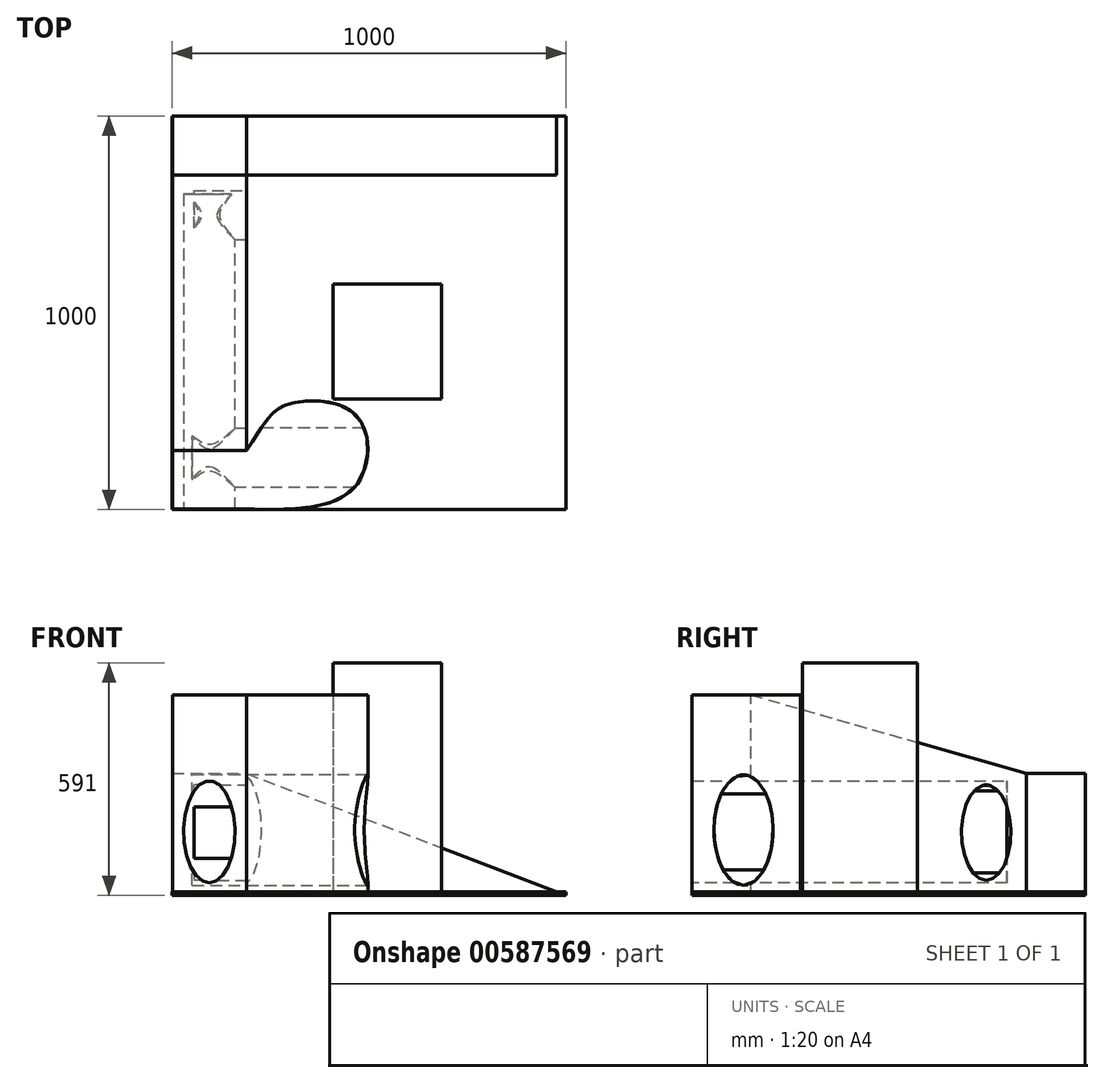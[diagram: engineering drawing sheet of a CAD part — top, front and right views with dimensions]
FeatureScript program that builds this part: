
annotation { "Feature Type Name" : "Feature", "Feature Type Description" : "" }
export const myFeature = defineFeature(function(context is Context, id is Id, definition is map)
    precondition{}
    {
        {
            var Q0;
            Q0=qCreatedBy(makeId("Top.planeOp"),FACE);
            var sketch = newSketch(context, id + "F0", { "sketchPlane" : qUnion([Q0])});
            skLineSegment(sketch, "E0.bottom", {"start": v(500, -500) * mm, "end": v(-500, -500) * mm});
            skLineSegment(sketch, "E0.top", {"start": v(500, 500) * mm, "end": v(-500, 500) * mm});
            skLineSegment(sketch, "E0.left", {"start": v(500, -500) * mm, "end": v(500, 500) * mm});
            skLineSegment(sketch, "E0.right", {"start": v(-500, -500) * mm, "end": v(-500, 500) * mm});
            skPoint(sketch, "E0.middle", {"position": v(0, 0) * mm});
            skSolve(sketch);
        }
        {
            var Q0;
            Q0=makeQuery(id+"F0.imprint","IMPRINT",FACE,{"disambiguationData":[TD([[makeQuery(id+"F0.imprint","IMPRINT",EDGE,{"derivedFrom":sQuery(id+"F0.wireOp",EDGE,"E0.bottom")}),-1.0]])]});
            extrude(context, id + "F1", {"entities" : qUnion([Q0]), "oppositeDirection" : true, "depth" : 10 * mm, "offsetDistance" : 25 * mm});
        }
        {
            var Q0;
            Q0=qCreatedBy(makeId("Front.planeOp"),FACE);
            cPlane(context, id + "F2", {"entities" : qUnion([Q0]), "cplaneType" : CPlaneType.OFFSET, "offset" : 500 * mm, "oppositeDirection" : true, "width" : 150 * mm, "height" : 150 * mm});
        }
        {
            var Q0;
            Q0=qCreatedBy(id+"F2.planeOp",FACE);
            var sketch = newSketch(context, id + "F3", { "sketchPlane" : qUnion([Q0])});
            skLineSegment(sketch, "E1", {"start": v(476.55, 0) * mm, "end": v(-310.9, 0) * mm});
            skLineSegment(sketch, "E2", {"start": v(-310.9, 0) * mm, "end": v(-310.9, 300) * mm});
            skLineSegment(sketch, "E3", {"start": v(-310.9, 300) * mm, "end": v(476.55, 0) * mm});
            skLineSegment(sketch, "E4", {"start": v(-310.9, 0) * mm, "end": v(-499.17, 0) * mm});
            skLineSegment(sketch, "E5", {"start": v(-499.17, 0) * mm, "end": v(-499.17, 300) * mm});
            skLineSegment(sketch, "E6", {"start": v(-499.17, 300) * mm, "end": v(-310.9, 300) * mm});
            skSolve(sketch);
        }
        {
            var Q0;
            Q0=makeQuery(id+"F3.imprint","IMPRINT",FACE,{"disambiguationData":[TD([[makeQuery(id+"F3.imprint","IMPRINT",EDGE,{"derivedFrom":sQuery(id+"F3.wireOp",EDGE,"E1")}),-1.0]])]});
            var Q1;
            Q1=makeQuery(id+"F3.imprint","IMPRINT",FACE,{"disambiguationData":[TD([[makeQuery(id+"F3.imprint","IMPRINT",EDGE,{"derivedFrom":sQuery(id+"F3.wireOp",EDGE,"E2")}),1.0]])]});
            extrude(context, id + "F4", {"entities" : qUnion([Q0, Q1]), "operationType" : NewBodyOperationType.ADD, "depth" : 150 * mm, "offsetDistance" : 25 * mm});
        }
        {
            var Q0;
            Q0=makeQuery(id+"F4.opExtrude","SWEPT_FACE",FACE,{"disambiguationData":[OSD([sQuery(id+"F3.wireOp",EDGE,"E5")])]});
            var sketch = newSketch(context, id + "F5", { "sketchPlane" : qUnion([Q0])});
            skLineSegment(sketch, "E7", {"start": v(-350, 300) * mm, "end": v(-350, 0) * mm});
            skLineSegment(sketch, "E8", {"start": v(-350, 0) * mm, "end": v(350, 0) * mm});
            skLineSegment(sketch, "E9", {"start": v(350, 0) * mm, "end": v(350, 500) * mm});
            skLineSegment(sketch, "E10", {"start": v(350, 500) * mm, "end": v(-350, 300) * mm});
            skLineSegment(sketch, "E11", {"start": v(350, 0) * mm, "end": v(499.02, 0) * mm});
            skLineSegment(sketch, "E12", {"start": v(499.02, 0) * mm, "end": v(499.02, 500) * mm});
            skLineSegment(sketch, "E13", {"start": v(499.02, 500) * mm, "end": v(350, 500) * mm});
            skSolve(sketch);
        }
        {
            var Q0;
            Q0=makeQuery(id+"F5.imprint","IMPRINT",FACE,{"disambiguationData":[TD([[makeQuery(id+"F5.imprint","IMPRINT",EDGE,{"derivedFrom":sQuery(id+"F5.wireOp",EDGE,"E7")}),-1.0]])]});
            var Q1;
            Q1=makeQuery(id+"F5.imprint","IMPRINT",FACE,{"disambiguationData":[TD([[makeQuery(id+"F5.imprint","IMPRINT",EDGE,{"derivedFrom":sQuery(id+"F5.wireOp",EDGE,"E9")}),-1.0]])]});
            extrude(context, id + "F6", {"entities" : qUnion([Q0, Q1]), "operationType" : NewBodyOperationType.ADD, "oppositeDirection" : true, "depth" : 188 * mm, "offsetDistance" : 25 * mm});
        }
        {
            var Q0;
            Q0=makeQuery(id+"F6.opExtrude","SWEPT_FACE",FACE,{"disambiguationData":[OSD([sQuery(id+"F5.wireOp",EDGE,"E13")])]});
            var sketch = newSketch(context, id + "F7", { "sketchPlane" : qUnion([Q0])});
            skFitSpline(sketch, "E14", {"points": [v(-311.17, -499.02) * mm, v(-35.43, -442.33) * mm, v(-31.14, -261.96) * mm, v(-185.74, -227.6) * mm, v(-239.42, -251.23) * mm, v(-267.33, -283.44) * mm, v(-311.17, -350) * mm], "startDerivative": vector(1320.7, -22.27) * mm, "endDerivative": vector(-342.1, -535.5) * mm});
            skSolve(sketch);
        }
        {
            var Q0;
            Q0=makeQuery(id+"F7.imprint","IMPRINT",FACE,{"disambiguationData":[TD([[makeQuery(id+"F7.imprint","IMPRINT",EDGE,{"derivedFrom":sQuery(id+"F7.wireOp",EDGE,"E14")}),1.0]])]});
            extrude(context, id + "F8", {"entities" : qUnion([Q0]), "operationType" : NewBodyOperationType.ADD, "oppositeDirection" : true, "depth" : 500 * mm, "offsetDistance" : 25 * mm});
        }
        {
            var Q0;
            Q0=makeQuery(id+"F6.opExtrude","CAP_FACE",FACE,{"disambiguationData":[OSD([sQuery(id+"F5.wireOp",EDGE,"E7"),sQuery(id+"F5.wireOp",EDGE,"E8"),sQuery(id+"F5.wireOp",EDGE,"E10"),sQuery(id+"F5.wireOp",EDGE,"E11"),sQuery(id+"F5.wireOp",EDGE,"E12"),sQuery(id+"F5.wireOp",EDGE,"E13")])],"isStart":false});
            cPlane(context, id + "F9", {"entities" : qUnion([Q0]), "cplaneType" : CPlaneType.OFFSET, "offset" : 315 * mm, "width" : 150 * mm, "height" : 150 * mm});
        }
        {
            var Q0;
            Q0=qCreatedBy(id+"F9.planeOp",FACE);
            var sketch = newSketch(context, id + "F10", { "sketchPlane" : qUnion([Q0])});
            skEllipse(sketch, "E15", {"center": v(-368.56, 156.63) * mm, "majorRadius": 140.2 * mm, "minorRadius": 75 * mm, "majorAxis": v(0, -1)});
            skSolve(sketch);
        }
        {
            var Q0;
            Q0=makeQuery(id+"F1.opExtrude","CAP_FACE",FACE,{"disambiguationData":[OSD([sQuery(id+"F0.wireOp",EDGE,"E0.bottom"),sQuery(id+"F0.wireOp",EDGE,"E0.top"),sQuery(id+"F0.wireOp",EDGE,"E0.left"),sQuery(id+"F0.wireOp",EDGE,"E0.right")])],"isStart":true});
            cPlane(context, id + "F11", {"entities" : qUnion([Q0]), "cplaneType" : CPlaneType.OFFSET, "offset" : 150 * mm, "width" : 150 * mm, "height" : 150 * mm});
        }
        {
            var Q0;
            Q0=makeQuery(id+"F10.imprint","IMPRINT",FACE,{"disambiguationData":[TD([[makeQuery(id+"F10.imprint","IMPRINT",EDGE,{"derivedFrom":sQuery(id+"F10.wireOp",EDGE,"E15")}),1.0]])]});
            extrude(context, id + "F12", {"entities" : qUnion([Q0]), "operationType" : NewBodyOperationType.REMOVE, "oppositeDirection" : true, "depth" : 453 * mm, "offsetDistance" : 25 * mm});
        }
        {
            var Q0;
            Q0=makeQuery(id+"F6.opExtrude","SWEPT_FACE",FACE,{"disambiguationData":[OSD([sQuery(id+"F5.wireOp",EDGE,"E12")])]});
            var sketch = newSketch(context, id + "F13", { "sketchPlane" : qUnion([Q0])});
            skEllipse(sketch, "E16", {"center": v(-405.59, 152) * mm, "majorRadius": 129.64 * mm, "minorRadius": 65 * mm, "majorAxis": v(0, -1)});
            skSolve(sketch);
        }
        {
            var Q0;
            Q0=makeQuery(id+"F13.imprint","IMPRINT",FACE,{"disambiguationData":[TD([[makeQuery(id+"F13.imprint","IMPRINT",EDGE,{"derivedFrom":sQuery(id+"F13.wireOp",EDGE,"E16")}),1.0]])]});
            extrude(context, id + "F14", {"entities" : qUnion([Q0]), "operationType" : NewBodyOperationType.REMOVE, "oppositeDirection" : true, "depth" : 800 * mm, "offsetDistance" : 25 * mm});
        }
        {
            var Q0;
            Q0=makeQuery(id+"F6.opExtrude","CAP_FACE",FACE,{"disambiguationData":[OSD([sQuery(id+"F5.wireOp",EDGE,"E7"),sQuery(id+"F5.wireOp",EDGE,"E8"),sQuery(id+"F5.wireOp",EDGE,"E10"),sQuery(id+"F5.wireOp",EDGE,"E11"),sQuery(id+"F5.wireOp",EDGE,"E12"),sQuery(id+"F5.wireOp",EDGE,"E13")])],"isStart":false});
            var sketch = newSketch(context, id + "F15", { "sketchPlane" : qUnion([Q0])});
            skEllipse(sketch, "E17", {"center": v(248, 150) * mm, "majorRadius": 121.18 * mm, "minorRadius": 62.72 * mm, "majorAxis": v(0, -1)});
            skPoint(sketch, "E17.centerSnap0", {"position": v(350, 150) * mm});
            skSolve(sketch);
        }
        {
            var Q0;
            Q0=makeQuery(id+"F15.imprint","IMPRINT",FACE,{"disambiguationData":[TD([[makeQuery(id+"F15.imprint","IMPRINT",EDGE,{"derivedFrom":sQuery(id+"F15.wireOp",EDGE,"E17")}),1.0]])]});
            extrude(context, id + "F16", {"entities" : qUnion([Q0]), "operationType" : NewBodyOperationType.REMOVE, "oppositeDirection" : true, "depth" : 133 * mm, "offsetDistance" : 25 * mm});
        }
        {
            var Q0;
            Q0=makeQuery(id+"F1.opExtrude","CAP_FACE",FACE,{"disambiguationData":[OSD([sQuery(id+"F0.wireOp",EDGE,"E0.bottom"),sQuery(id+"F0.wireOp",EDGE,"E0.top"),sQuery(id+"F0.wireOp",EDGE,"E0.left"),sQuery(id+"F0.wireOp",EDGE,"E0.right")])],"isStart":true});
            var sketch = newSketch(context, id + "F17", { "sketchPlane" : qUnion([Q0])});
            skLineSegment(sketch, "E18.bottom", {"start": v(183.59, -219.02) * mm, "end": v(-91.26, -219.02) * mm});
            skLineSegment(sketch, "E18.top", {"start": v(183.59, 73) * mm, "end": v(-91.26, 73) * mm});
            skLineSegment(sketch, "E18.left", {"start": v(183.59, -219.02) * mm, "end": v(183.59, 73) * mm});
            skLineSegment(sketch, "E18.right", {"start": v(-91.26, -219.02) * mm, "end": v(-91.26, 73) * mm});
            skPoint(sketch, "E18.middle", {"position": v(46.17, -73) * mm});
            skLineSegment(sketch, "E19.bottom", {"start": v(-35.43, -468.1) * mm, "end": v(479.9, -468.1) * mm});
            skLineSegment(sketch, "E19.top", {"start": v(-35.43, -476.69) * mm, "end": v(479.9, -476.69) * mm});
            skLineSegment(sketch, "E19.left", {"start": v(-35.43, -468.1) * mm, "end": v(-35.43, -476.69) * mm});
            skLineSegment(sketch, "E19.right", {"start": v(479.9, -468.1) * mm, "end": v(479.9, -476.69) * mm});
            skSolve(sketch);
        }
        {
            var Q0;
            Q0=makeQuery(id+"F17.imprint","IMPRINT",FACE,{"disambiguationData":[TD([[makeQuery(id+"F17.imprint","IMPRINT",EDGE,{"derivedFrom":sQuery(id+"F17.wireOp",EDGE,"E18.bottom")}),-1.0]])]});
            extrude(context, id + "F18", {"entities" : qUnion([Q0]), "operationType" : NewBodyOperationType.ADD, "depth" : 581 * mm, "offsetDistance" : 25 * mm});
        }
        {
            var Q0;
            Q0=sQuery(id+"F17.wireOp",EDGE,"E19.top");
            extrude(context, id + "F19", {"bodyType" : ToolBodyType.SURFACE, "surfaceEntities" : qUnion([Q0]), "depth" : 335 * mm, "offsetDistance" : 25 * mm});
        }
    });
